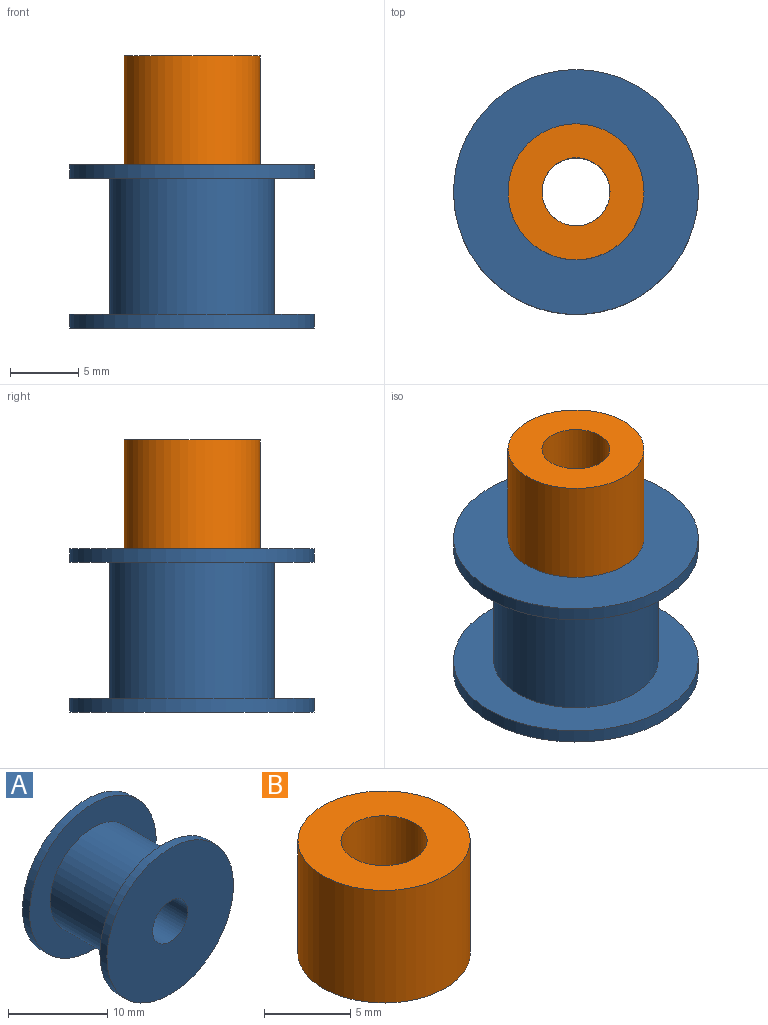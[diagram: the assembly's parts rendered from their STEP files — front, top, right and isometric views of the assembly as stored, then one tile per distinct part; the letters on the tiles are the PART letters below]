
ASSEMBLY  parts=2 mates=1
PART A: 8 faces, bbox 18x12x18 mm
  f0: plane 18x18mm, normal (0,1,0), area 234.8mm2, adj f6,f7
  f1: plane 18x18mm, normal (0,-1,0), area 234.8mm2, adj f2,f7
  f2: cylinder r=9mm len=18mm, axis (0,-1,0), area 56.5mm2, adj f1,f3
  f3: plane 18x18mm, normal (0,1,0), area 139.5mm2, adj f2,f4
  f4: cylinder r=6.05mm len=12.1mm, axis (0,-1,0), area 380.1mm2, adj f3,f5
  f5: plane 18x18mm, normal (0,-1,0), area 139.5mm2, adj f4,f6
  f6: cylinder r=9mm len=18mm, axis (0,-1,0), area 56.5mm2, adj f0,f5
  f7: cylinder r=2.5mm len=12mm, axis (0,1,0), area 188.5mm2, adj f0,f1
PART B: 4 faces, bbox 10x10x8 mm
  f0: cylinder r=2.5mm len=8mm, axis (0,0,-1), area 125.7mm2, adj f2,f3
  f1: cylinder r=5mm len=10mm, axis (0,0,-1), area 251.3mm2, adj f2,f3
  f2: plane 10x10mm, normal (0,0,1), area 58.9mm2, adj f0,f1
  f3: plane 10x10mm, normal (0,0,-1), area 58.9mm2, adj f0,f1
PLACE A rot(axis=(1,0,0),90deg) t=(-6.76,-1.67,7.19)mm
PLACE B t=(-6.76,-1.67,7.19)mm
MATE fastened A.f2 <-> B.f0  axis (0,0,1) through (-6.76,-1.67,7.19)mm
